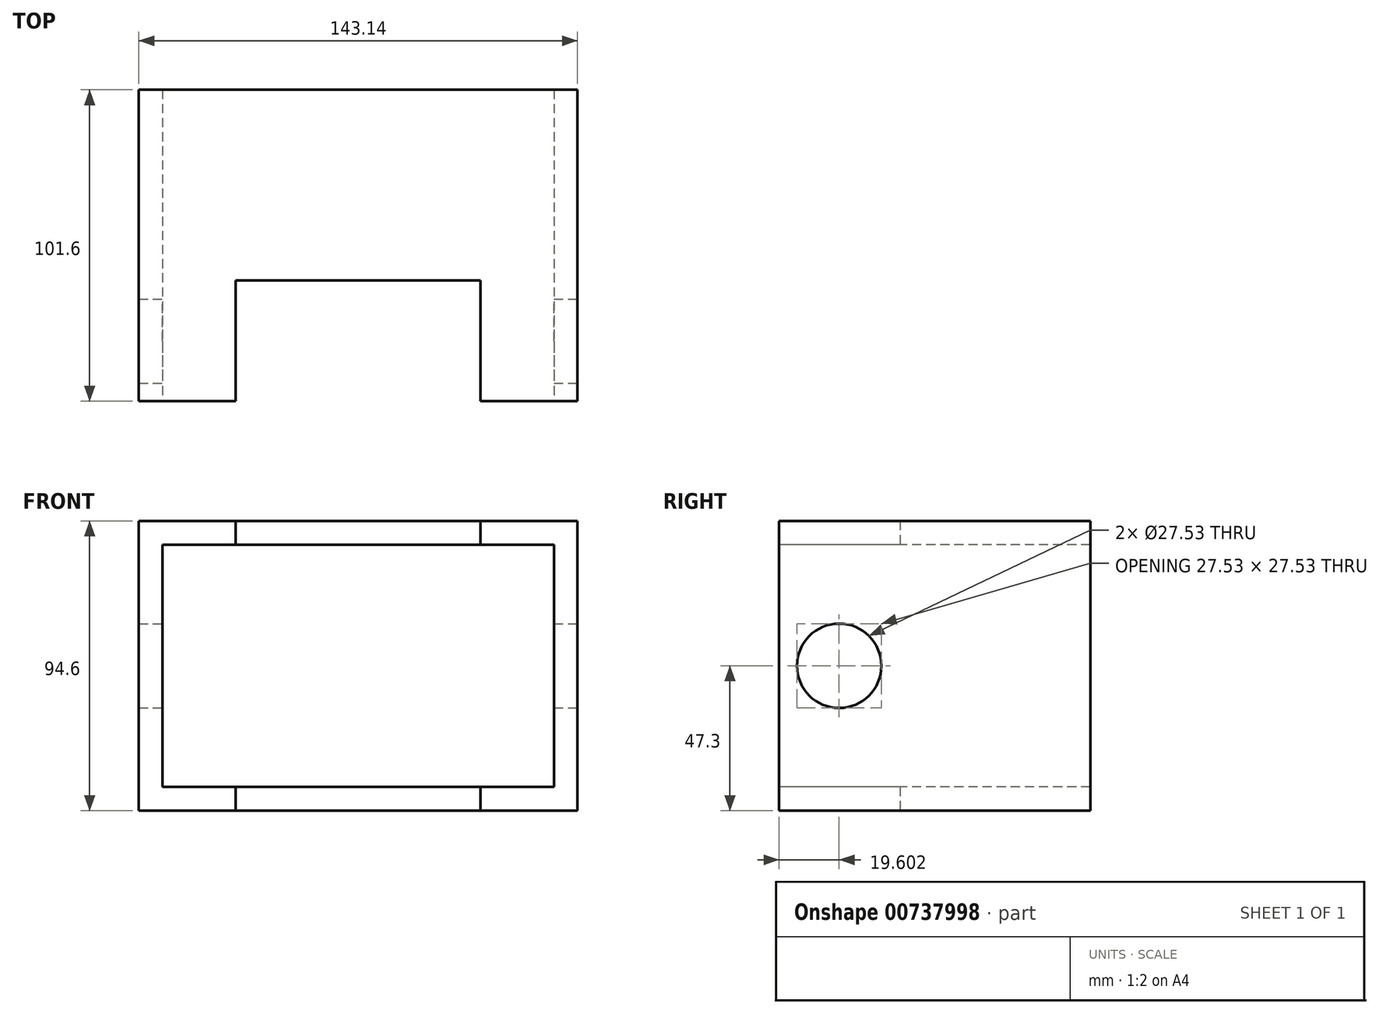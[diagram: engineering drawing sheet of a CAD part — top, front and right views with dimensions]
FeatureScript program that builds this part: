
annotation { "Feature Type Name" : "Feature", "Feature Type Description" : "" }
export const myFeature = defineFeature(function(context is Context, id is Id, definition is map)
    precondition{}
    {
        {
            var Q0;
            Q0=qCreatedBy(makeId("Front.planeOp"),FACE);
            var sketch = newSketch(context, id + "F0", { "sketchPlane" : qUnion([Q0])});
            skLineSegment(sketch, "E0.bottom", {"start": v(71.57, 47.3) * mm, "end": v(-71.57, 47.3) * mm});
            skLineSegment(sketch, "E0.top", {"start": v(71.57, -47.3) * mm, "end": v(-71.57, -47.3) * mm});
            skLineSegment(sketch, "E0.left", {"start": v(71.57, 47.3) * mm, "end": v(71.57, -47.3) * mm});
            skLineSegment(sketch, "E0.right", {"start": v(-71.57, 47.3) * mm, "end": v(-71.57, -47.3) * mm});
            skPoint(sketch, "E0.middle", {"position": v(0, 0) * mm});
            skSolve(sketch);
        }
        {
            var Q0;
            Q0=makeQuery(id+"F0.imprint","IMPRINT",FACE,{"disambiguationData":[TD([[makeQuery(id+"F0.imprint","IMPRINT",EDGE,{"derivedFrom":sQuery(id+"F0.wireOp",EDGE,"E0.bottom")}),1.0]])]});
            extrude(context, id + "F1", {"entities" : qUnion([Q0]), "depth" : 101.6 * mm, "offsetDistance" : 25.4 * mm});
        }
        {
            var Q0;
            Q0=makeQuery(id+"F1.opExtrude","CAP_FACE",FACE,{"disambiguationData":[OSD([sQuery(id+"F0.wireOp",EDGE,"E0.bottom"),sQuery(id+"F0.wireOp",EDGE,"E0.top"),sQuery(id+"F0.wireOp",EDGE,"E0.left"),sQuery(id+"F0.wireOp",EDGE,"E0.right")])],"isStart":false});
            var sketch = newSketch(context, id + "F2", { "sketchPlane" : qUnion([Q0])});
            skLineSegment(sketch, "E1.bottom", {"start": v(63.9, 39.53) * mm, "end": v(-63.9, 39.53) * mm});
            skLineSegment(sketch, "E1.top", {"start": v(63.9, -39.53) * mm, "end": v(-63.9, -39.53) * mm});
            skLineSegment(sketch, "E1.left", {"start": v(63.9, 39.53) * mm, "end": v(63.9, -39.53) * mm});
            skLineSegment(sketch, "E1.right", {"start": v(-63.9, 39.53) * mm, "end": v(-63.9, -39.53) * mm});
            skPoint(sketch, "E1.middle", {"position": v(0, 0) * mm});
            skSolve(sketch);
        }
        {
            var Q0;
            Q0 = qSketchRegion(id + "F2", true);
            extrude(context, id + "F3", {"entities" : qUnion([Q0]), "operationType" : NewBodyOperationType.REMOVE, "oppositeDirection" : true, "depth" : 127 * mm, "offsetDistance" : 25.4 * mm});
        }
        {
            var Q0;
            Q0=makeQuery(id+"F1.opExtrude","SWEPT_FACE",FACE,{"disambiguationData":[OSD([sQuery(id+"F0.wireOp",EDGE,"E0.top")])]});
            var sketch = newSketch(context, id + "F4", { "sketchPlane" : qUnion([Q0])});
            skLineSegment(sketch, "E2.bottom", {"start": v(39.97, 101.6) * mm, "end": v(-39.97, 101.6) * mm});
            skLineSegment(sketch, "E2.top", {"start": v(39.97, 62.14) * mm, "end": v(-39.97, 62.14) * mm});
            skLineSegment(sketch, "E2.left", {"start": v(39.97, 101.6) * mm, "end": v(39.97, 62.14) * mm});
            skLineSegment(sketch, "E2.right", {"start": v(-39.97, 101.6) * mm, "end": v(-39.97, 62.14) * mm});
            skPoint(sketch, "E2.middle", {"position": v(0, 81.87) * mm});
            skPoint(sketch, "E2.middle.positionSnap0", {"position": v(0, 101.6) * mm});
            skPoint(sketch, "E2.centerSnap0", {"position": v(0, 101.6) * mm});
            skSolve(sketch);
        }
        {
            var Q0;
            Q0 = qSketchRegion(id + "F4", true);
            extrude(context, id + "F5", {"entities" : qUnion([Q0]), "operationType" : NewBodyOperationType.REMOVE, "oppositeDirection" : true, "depth" : 127 * mm, "offsetDistance" : 25.4 * mm});
        }
        {
            var Q0;
            Q0=makeQuery(id+"F1.opExtrude","SWEPT_FACE",FACE,{"disambiguationData":[OSD([sQuery(id+"F0.wireOp",EDGE,"E0.left")])]});
            var sketch = newSketch(context, id + "F6", { "sketchPlane" : qUnion([Q0])});
            skCircle(sketch, "E3", {"center": v(-82, 0) * mm, "radius": 13.77 * mm});
            skPoint(sketch, "E3.centerSnap0", {"position": v(-101.6, 0) * mm});
            skSolve(sketch);
        }
        {
            var Q0;
            Q0 = qSketchRegion(id + "F6", true);
            extrude(context, id + "F7", {"entities" : qUnion([Q0]), "operationType" : NewBodyOperationType.REMOVE, "oppositeDirection" : true, "depth" : 152.4 * mm, "offsetDistance" : 25.4 * mm});
        }
    });
